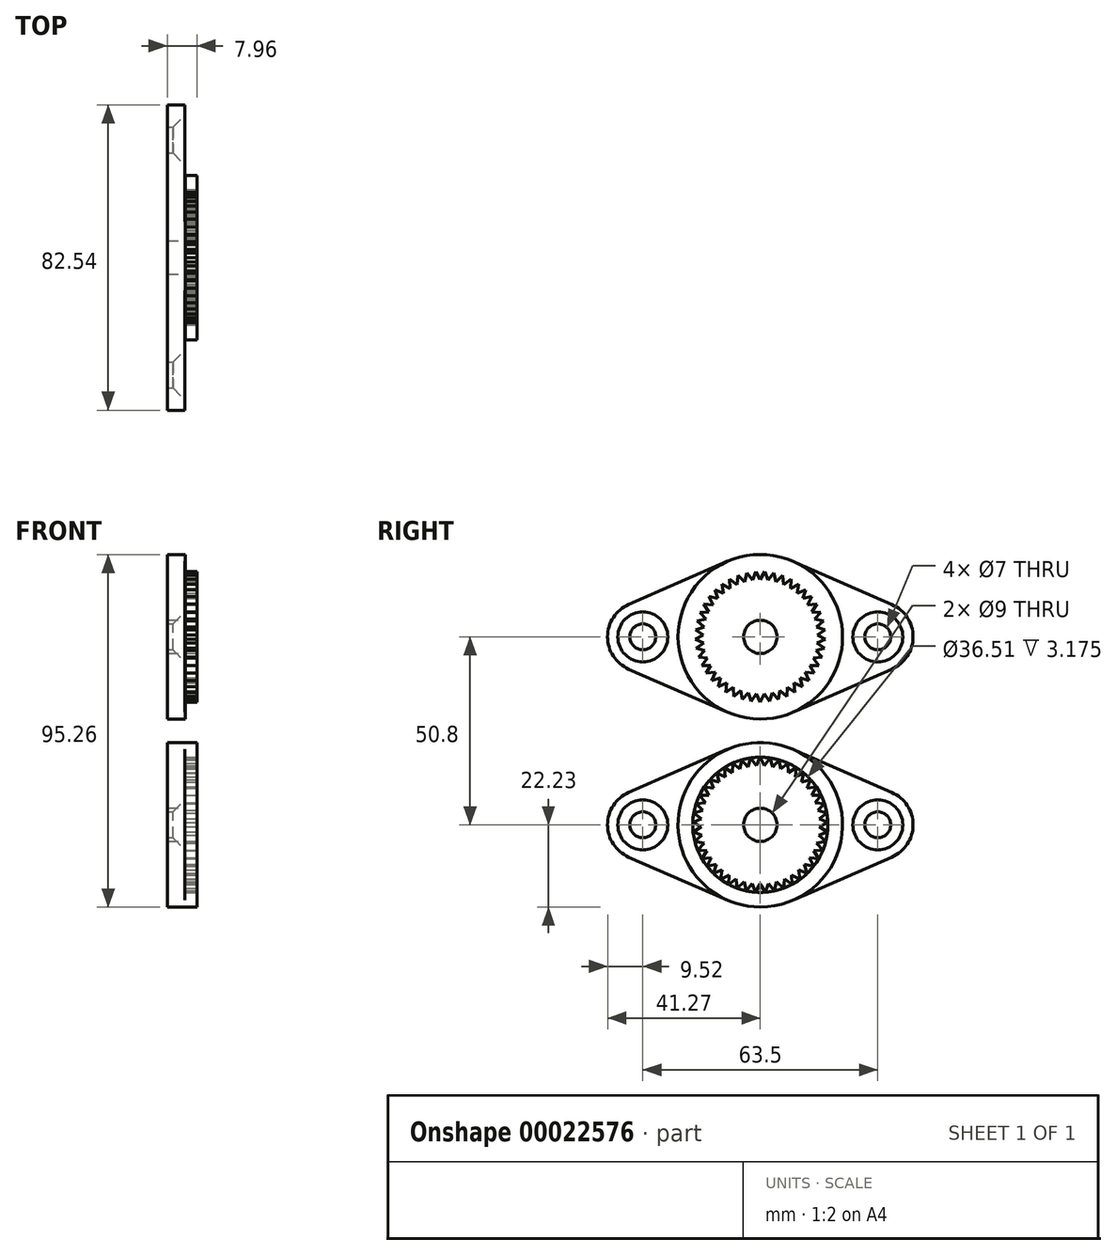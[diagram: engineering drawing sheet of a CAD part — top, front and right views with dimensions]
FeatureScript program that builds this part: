
annotation { "Feature Type Name" : "Feature", "Feature Type Description" : "" }
export const myFeature = defineFeature(function(context is Context, id is Id, definition is map)
    precondition{}
    {
        {
            var Q0;
            Q0=qCreatedBy(makeId("Right.planeOp"),FACE);
            var sketch = newSketch(context, id + "F0", { "sketchPlane" : qUnion([Q0])});
            skArc(sketch, "E0", {"start": v(-8.9, -20.37) * mm, "mid": v(0, -22.23) * mm, "end": v(8.9, -20.37) * mm});
            skLineSegment(sketch, "E1", {"start": v(-77.57, 0) * mm, "end": v(77.57, 0) * mm, "construction": true});
            skArc(sketch, "E2", {"start": v(-35.56, 8.73) * mm, "mid": v(-41.28, 0) * mm, "end": v(-35.56, -8.73) * mm});
            skArc(sketch, "E3", {"start": v(35.56, -8.73) * mm, "mid": v(41.27, 0) * mm, "end": v(35.56, 8.73) * mm});
            skLineSegment(sketch, "E4", {"start": v(-35.56, 8.73) * mm, "end": v(-8.89, 20.37) * mm});
            skLineSegment(sketch, "E5", {"start": v(-35.56, -8.73) * mm, "end": v(-8.9, -20.37) * mm});
            skLineSegment(sketch, "E6", {"start": v(35.56, -8.73) * mm, "end": v(8.9, -20.37) * mm});
            skLineSegment(sketch, "E7", {"start": v(35.56, 8.73) * mm, "end": v(8.89, 20.37) * mm});
            skArc(sketch, "E8.trimOffspring", {"start": v(8.9, 20.37) * mm, "mid": v(0, 22.22) * mm, "end": v(-8.9, 20.37) * mm});
            skLineSegment(sketch, "E9", {"start": v(-41.27, 0) * mm, "end": v(41.27, 0) * mm, "construction": true});
            skSolve(sketch);
        }
        {
            var Q0;
            Q0=qSketchRegion(id+"F0",true);
            extrude(context, id + "F1", {"entities" : qUnion([Q0]), "depth" : 4.76 * mm});
        }
        {
            var Q0;
            Q0=makeQuery(id+"F1.opExtrude","CAP_FACE",FACE,{"disambiguationData":[OSD([sQuery(id+"F0.wireOp",EDGE,"E0"),sQuery(id+"F0.wireOp",EDGE,"E2"),sQuery(id+"F0.wireOp",EDGE,"E3"),sQuery(id+"F0.wireOp",EDGE,"E4"),sQuery(id+"F0.wireOp",EDGE,"E5"),sQuery(id+"F0.wireOp",EDGE,"E6"),sQuery(id+"F0.wireOp",EDGE,"E7"),sQuery(id+"F0.wireOp",EDGE,"E8.trimOffspring")])],"isStart":false});
            var sketch = newSketch(context, id + "F2", { "sketchPlane" : qUnion([Q0])});
            skCircle(sketch, "E10", {"center": v(0, 0) * mm, "radius": 22.23 * mm});
            skSolve(sketch);
        }
        {
            var Q0;
            Q0=qSketchRegion(id+"F2",true);
            extrude(context, id + "F3", {"entities" : qUnion([Q0]), "operationType" : NewBodyOperationType.ADD, "depth" : 0.03 * mm});
        }
        {
            var Q0;
            Q0=qCreatedBy(makeId("Top.planeOp"),FACE);
            cPlane(context, id + "F4", {"entities" : qUnion([Q0]), "cplaneType" : CPlaneType.OFFSET, "offset" : 19.05 * mm, "width" : 152.4 * mm, "height" : 152.4 * mm});
        }
        {
            var Q0;
            Q0=qCreatedBy(makeId("Top.planeOp"),FACE);
            cPlane(context, id + "F5", {"entities" : qUnion([Q0]), "cplaneType" : CPlaneType.OFFSET, "offset" : 6.35 * mm, "width" : 152.4 * mm, "height" : 152.4 * mm});
        }
        {
            var Q0;
            Q0=qCreatedBy(id+"F4.planeOp",FACE);
            var sketch = newSketch(context, id + "F6", { "sketchPlane" : qUnion([Q0])});
            skLineSegment(sketch, "E11", {"start": v(0, 0) * mm, "end": v(4.79, 0) * mm, "construction": true});
            skLineSegment(sketch, "E12", {"start": v(4.79, 0.8) * mm, "end": v(4.79, -0.8) * mm});
            skLineSegment(sketch, "E13", {"start": v(4.79, 0) * mm, "end": v(5.8, 0) * mm, "construction": true});
            skLineSegment(sketch, "E14", {"start": v(4.79, -0.8) * mm, "end": v(5.8, 0) * mm});
            skLineSegment(sketch, "E15", {"start": v(4.79, 0.8) * mm, "end": v(5.8, 0) * mm});
            skSolve(sketch);
        }
        {
            var Q0;
            Q0=qCreatedBy(id+"F5.planeOp",FACE);
            var sketch = newSketch(context, id + "F7", { "sketchPlane" : qUnion([Q0])});
            skLineSegment(sketch, "E16", {"start": v(4.79, -0.25) * mm, "end": v(4.79, 0.25) * mm});
            skLineSegment(sketch, "E17", {"start": v(-1.93, 0) * mm, "end": v(4.79, 0) * mm, "construction": true});
            skLineSegment(sketch, "E18", {"start": v(4.79, 0) * mm, "end": v(5.8, 0) * mm, "construction": true});
            skLineSegment(sketch, "E19", {"start": v(5.8, 0) * mm, "end": v(4.79, 0.25) * mm});
            skLineSegment(sketch, "E20", {"start": v(5.8, 0) * mm, "end": v(4.79, -0.25) * mm});
            skSolve(sketch);
        }
        {
            var Q0;
            {var subQ0=sQuery(id+"F0.wireOp",EDGE,"E0");var subQ1=sQuery(id+"F0.wireOp",EDGE,"E3");var subQ2=sQuery(id+"F0.wireOp",EDGE,"E6");var subQ3=sQuery(id+"F0.wireOp",EDGE,"E7");var subQ4=sQuery(id+"F0.wireOp",EDGE,"E8.trimOffspring");Q0=makeQuery(id+"F3.boolean.opBoolean","SPLIT",FACE,{"disambiguationData":[TD([makeQuery(id+"F1.opExtrude","SWEPT_FACE",FACE,{"disambiguationData":[OSD([subQ1])]})])],"derivedFrom":makeQuery(id+"F1.opExtrude","CAP_FACE",FACE,{"disambiguationData":[OSD([subQ0,sQuery(id+"F0.wireOp",EDGE,"E2"),subQ1,sQuery(id+"F0.wireOp",EDGE,"E4"),sQuery(id+"F0.wireOp",EDGE,"E5"),subQ2,subQ3,subQ4])],"isStart":false})});}
            var sketch = newSketch(context, id + "F8", { "sketchPlane" : qUnion([Q0])});
            skCircle(sketch, "E21", {"center": v(31.75, 0) * mm, "radius": 3.5 * mm});
            skCircle(sketch, "E22", {"center": v(-31.75, 0) * mm, "radius": 3.5 * mm});
            skCircle(sketch, "E23", {"center": v(0, 0) * mm, "radius": 4.5 * mm});
            skSolve(sketch);
        }
        {
            var Q0;
            Q0=qSketchRegion(id+"F8",true);
            extrude(context, id + "F9", {"entities" : qUnion([Q0]), "operationType" : NewBodyOperationType.REMOVE, "endBound" : BoundingType.SYMMETRIC, "oppositeDirection" : true, "depth" : 25.4 * mm});
        }
        {
            var Q0;
            Q0=makeQuery(id+"F8.imprint","IMPRINT",FACE,{"disambiguationData":[TD([[makeQuery(id+"F8.imprint","IMPRINT",EDGE,{"derivedFrom":sQuery(id+"F8.wireOp",EDGE,"E21")}),-1.0]])]});
            var sketch = newSketch(context, id + "F10", { "sketchPlane" : qUnion([Q0])});
            skCircle(sketch, "E24", {"center": v(31.75, 0) * mm, "radius": 6.75 * mm});
            skCircle(sketch, "E25", {"center": v(-31.75, 0) * mm, "radius": 6.75 * mm});
            skSolve(sketch);
        }
        {
            var Q0;
            Q0=qSketchRegion(id+"F10",true);
            extrude(context, id + "F11", {"entities" : qUnion([Q0]), "operationType" : NewBodyOperationType.REMOVE, "oppositeDirection" : true, "depth" : 25.4 * mm, "hasDraft" : true, "draftAngle" : 45 * degree, "draftPullDirection" : true});
        }
        {
            var Q0;
            {var subQ0=sQuery(id+"F2.wireOp",EDGE,"E10");var subQ3=sQuery(id+"F0.wireOp",EDGE,"E6");Q0=makeQuery(id+"F3.boolean.opBoolean","SPLIT",EDGE,{"disambiguationData":[TD([makeQuery(id+"F1.opExtrude","SWEPT_FACE",FACE,{"disambiguationData":[OSD([subQ3])]})])],"derivedFrom":makeQuery(id+"F3.opExtrude","CAP_EDGE",EDGE,{"disambiguationData":[OSD([subQ0])],"isStart":true})});}
            var Q1;
            {var subQ0=sQuery(id+"F2.wireOp",EDGE,"E10");var subQ3=sQuery(id+"F0.wireOp",EDGE,"E4");Q1=makeQuery(id+"F3.boolean.opBoolean","SPLIT",EDGE,{"disambiguationData":[TD([makeQuery(id+"F1.opExtrude","SWEPT_FACE",FACE,{"disambiguationData":[OSD([subQ3])]})])],"derivedFrom":makeQuery(id+"F3.opExtrude","CAP_EDGE",EDGE,{"disambiguationData":[OSD([subQ0])],"isStart":true})});}
            fillet(context, id + "F12", {"entities" : qUnion([Q0, Q1]), "radius" : 0.8 * mm, "allowEdgeOverflow" : false});
        }
        {
            var Q0;
            Q0=makeQuery(id+"F3.opExtrude","CAP_FACE",FACE,{"disambiguationData":[OSD([sQuery(id+"F2.wireOp",EDGE,"E10")])],"isStart":false});
            var sketch = newSketch(context, id + "F13", { "sketchPlane" : qUnion([Q0])});
            skCircle(sketch, "E26", {"center": v(0, 0) * mm, "radius": 18.26 * mm});
            skCircle(sketch, "E27", {"center": v(0, 0) * mm, "radius": 22.23 * mm});
            skSolve(sketch);
        }
        {
            var Q0;
            Q0 = qSketchRegion(id + "F13", true);
            extrude(context, id + "F14", {"entities" : qUnion([Q0]), "operationType" : NewBodyOperationType.ADD, "depth" : 3.17 * mm});
        }
        {
            var Q0;
            Q0=makeQuery(id+"F1.opExtrude","SWEPT_BODY",BODY,{"disambiguationData":[OSD([sQuery(id+"F0.wireOp",EDGE,"E0"),sQuery(id+"F0.wireOp",EDGE,"E2"),sQuery(id+"F0.wireOp",EDGE,"E3"),sQuery(id+"F0.wireOp",EDGE,"E4"),sQuery(id+"F0.wireOp",EDGE,"E5"),sQuery(id+"F0.wireOp",EDGE,"E6"),sQuery(id+"F0.wireOp",EDGE,"E7"),sQuery(id+"F0.wireOp",EDGE,"E8.trimOffspring")])]});
            transform(context, id + "F15", {"entities" : qUnion([Q0]), "transformType" : TransformType.TRANSLATION_3D, "dx" : 0 * mm, "dy" : 0 * mm, "dz" : 50.8 * mm, "makeCopy" : true});
        }
        {
            var Q0;
            Q0=makeQuery(id+"F15.opPattern","COPY",FACE,{"derivedFrom":makeQuery(id+"F3.opExtrude","CAP_FACE",FACE,{"disambiguationData":[OSD([sQuery(id+"F2.wireOp",EDGE,"E10")])],"isStart":false}),"instanceName":"1"});
            var sketch = newSketch(context, id + "F16", { "sketchPlane" : qUnion([Q0])});
            skCircle(sketch, "E28", {"center": v(0, 50.8) * mm, "radius": 17.62 * mm});
            skCircle(sketch, "E29", {"center": v(0, 50.8) * mm, "radius": 4.5 * mm});
            skSolve(sketch);
        }
        {
            var Q0;
            Q0=makeQuery(id+"F15.opPattern","COPY",FACE,{"derivedFrom":makeQuery(id+"F14.opExtrude","CAP_FACE",FACE,{"disambiguationData":[OSD([sQuery(id+"F13.wireOp",EDGE,"E26"),sQuery(id+"F13.wireOp",EDGE,"E27")])],"isStart":false}),"instanceName":"1"});
            var sketch = newSketch(context, id + "F17", { "sketchPlane" : qUnion([Q0])});
            skCircle(sketch, "E30", {"center": v(0, 50.8) * mm, "radius": 18.26 * mm});
            skCircle(sketch, "E31", {"center": v(0, 50.8) * mm, "radius": 22.23 * mm});
            skSolve(sketch);
        }
        {
            var Q0;
            Q0 = qSketchRegion(id + "F17", true);
            var Q1;
            Q1=makeQuery(id+"F15.opPattern","COPY",FACE,{"derivedFrom":makeQuery(id+"F3.opExtrude","CAP_FACE",FACE,{"disambiguationData":[OSD([sQuery(id+"F2.wireOp",EDGE,"E10")])],"isStart":false}),"instanceName":"1"});
            extrude(context, id + "F18", {"entities" : qUnion([Q0]), "operationType" : NewBodyOperationType.REMOVE, "endBound" : BoundingType.UP_TO_SURFACE, "oppositeDirection" : true, "endBoundEntityFace" : qUnion([Q1]), "depth" : 25.4 * mm});
        }
        {
            var Q0;
            Q0 = qSketchRegion(id + "F16", true);
            extrude(context, id + "F19", {"entities" : qUnion([Q0]), "operationType" : NewBodyOperationType.ADD, "depth" : 3.17 * mm});
        }
        {
            var Q0;
            Q0=makeQuery(id+"F19.opExtrude","CAP_FACE",FACE,{"disambiguationData":[OSD([sQuery(id+"F16.wireOp",EDGE,"E28"),sQuery(id+"F16.wireOp",EDGE,"E29")])],"isStart":false});
            var sketch = newSketch(context, id + "F20", { "sketchPlane" : qUnion([Q0])});
            skLineSegment(sketch, "E32", {"start": v(0, 50.8) * mm, "end": v(0, 70.91) * mm, "construction": true});
            skArc(sketch, "E33", {"start": v(1.23, 68.38) * mm, "mid": v(0, 68.42) * mm, "end": v(-1.23, 68.38) * mm});
            skLineSegment(sketch, "E34", {"start": v(1.23, 68.38) * mm, "end": v(0, 50.8) * mm, "construction": true});
            skLineSegment(sketch, "E35", {"start": v(-1.23, 68.38) * mm, "end": v(0, 50.8) * mm, "construction": true});
            skLineSegment(sketch, "E36", {"start": v(1.23, 68.38) * mm, "end": v(0, 66.25) * mm});
            skLineSegment(sketch, "E37", {"start": v(0, 66.25) * mm, "end": v(-1.23, 68.38) * mm});
            skPoint(sketch, "E38.center", {"position": v(0, 0) * mm});
            skSolve(sketch);
        }
        {
            var Q0;
            Q0 = qSketchRegion(id + "F20", true);
            var Q1;
            Q1=makeQuery(id+"F18.boolean.opBoolean","MERGE",FACE,{"derivedFrom":[makeQuery(id+"F15.opPattern","COPY",FACE,{"derivedFrom":makeQuery(id+"F3.opExtrude","CAP_FACE",FACE,{"disambiguationData":[OSD([sQuery(id+"F2.wireOp",EDGE,"E10")])],"isStart":false}),"instanceName":"1"})],"fromTools":[makeQuery(id+"F18.opExtrude","CAP_FACE",FACE,{"disambiguationData":[OSD([sQuery(id+"F17.wireOp",EDGE,"E30"),sQuery(id+"F17.wireOp",EDGE,"E31")])],"isStart":false})]});
            extrude(context, id + "F21", {"entities" : qUnion([Q0]), "endBound" : BoundingType.UP_TO_SURFACE, "oppositeDirection" : true, "endBoundEntityFace" : qUnion([Q1]), "depth" : 25.4 * mm});
        }
        {
            var Q0;
            Q0=makeQuery(id+"F21.opExtrude","SWEPT_BODY",BODY,{"disambiguationData":[OSD([sQuery(id+"F20.wireOp",EDGE,"E33"),sQuery(id+"F20.wireOp",EDGE,"E36"),sQuery(id+"F20.wireOp",EDGE,"E37")])]});
            var Q1;
            Q1=makeQuery(id+"F19.opExtrude","CAP_EDGE",EDGE,{"disambiguationData":[OSD([sQuery(id+"F16.wireOp",EDGE,"E29")])],"isStart":false});
            circularPattern(context, id + "F22", {"entities" : qUnion([Q0]), "axis" : qUnion([Q1]), "angle" : 360 * degree, "instanceCount" : 45, "equalSpace" : true});
        }
        {
            var Q0;
            Q0=makeQuery(id+"F21.opExtrude","SWEPT_BODY",BODY,{"disambiguationData":[OSD([sQuery(id+"F20.wireOp",EDGE,"E33"),sQuery(id+"F20.wireOp",EDGE,"E36"),sQuery(id+"F20.wireOp",EDGE,"E37")])]});
            var Q1;
            Q1=makeQuery(id+"F22.opPattern","COPY",BODY,{"derivedFrom":makeQuery(id+"F21.opExtrude","SWEPT_BODY",BODY,{"disambiguationData":[OSD([sQuery(id+"F20.wireOp",EDGE,"E33"),sQuery(id+"F20.wireOp",EDGE,"E36"),sQuery(id+"F20.wireOp",EDGE,"E37")])]}),"instanceName":"71"});
            var Q2;
            Q2=makeQuery(id+"F22.opPattern","COPY",BODY,{"derivedFrom":makeQuery(id+"F21.opExtrude","SWEPT_BODY",BODY,{"disambiguationData":[OSD([sQuery(id+"F20.wireOp",EDGE,"E33"),sQuery(id+"F20.wireOp",EDGE,"E36"),sQuery(id+"F20.wireOp",EDGE,"E37")])]}),"instanceName":"70"});
            var Q3;
            Q3=makeQuery(id+"F22.opPattern","COPY",BODY,{"derivedFrom":makeQuery(id+"F21.opExtrude","SWEPT_BODY",BODY,{"disambiguationData":[OSD([sQuery(id+"F20.wireOp",EDGE,"E33"),sQuery(id+"F20.wireOp",EDGE,"E36"),sQuery(id+"F20.wireOp",EDGE,"E37")])]}),"instanceName":"68"});
            var Q4;
            Q4=makeQuery(id+"F22.opPattern","COPY",BODY,{"derivedFrom":makeQuery(id+"F21.opExtrude","SWEPT_BODY",BODY,{"disambiguationData":[OSD([sQuery(id+"F20.wireOp",EDGE,"E33"),sQuery(id+"F20.wireOp",EDGE,"E36"),sQuery(id+"F20.wireOp",EDGE,"E37")])]}),"instanceName":"69"});
            var Q5;
            Q5=makeQuery(id+"F22.opPattern","COPY",BODY,{"derivedFrom":makeQuery(id+"F21.opExtrude","SWEPT_BODY",BODY,{"disambiguationData":[OSD([sQuery(id+"F20.wireOp",EDGE,"E33"),sQuery(id+"F20.wireOp",EDGE,"E36"),sQuery(id+"F20.wireOp",EDGE,"E37")])]}),"instanceName":"67"});
            var Q6;
            Q6=makeQuery(id+"F22.opPattern","COPY",BODY,{"derivedFrom":makeQuery(id+"F21.opExtrude","SWEPT_BODY",BODY,{"disambiguationData":[OSD([sQuery(id+"F20.wireOp",EDGE,"E33"),sQuery(id+"F20.wireOp",EDGE,"E36"),sQuery(id+"F20.wireOp",EDGE,"E37")])]}),"instanceName":"1"});
            var Q7;
            Q7=makeQuery(id+"F22.opPattern","COPY",BODY,{"derivedFrom":makeQuery(id+"F21.opExtrude","SWEPT_BODY",BODY,{"disambiguationData":[OSD([sQuery(id+"F20.wireOp",EDGE,"E33"),sQuery(id+"F20.wireOp",EDGE,"E36"),sQuery(id+"F20.wireOp",EDGE,"E37")])]}),"instanceName":"2"});
            var Q8;
            Q8=makeQuery(id+"F22.opPattern","COPY",BODY,{"derivedFrom":makeQuery(id+"F21.opExtrude","SWEPT_BODY",BODY,{"disambiguationData":[OSD([sQuery(id+"F20.wireOp",EDGE,"E33"),sQuery(id+"F20.wireOp",EDGE,"E36"),sQuery(id+"F20.wireOp",EDGE,"E37")])]}),"instanceName":"66"});
            var Q9;
            Q9=makeQuery(id+"F22.opPattern","COPY",BODY,{"derivedFrom":makeQuery(id+"F21.opExtrude","SWEPT_BODY",BODY,{"disambiguationData":[OSD([sQuery(id+"F20.wireOp",EDGE,"E33"),sQuery(id+"F20.wireOp",EDGE,"E36"),sQuery(id+"F20.wireOp",EDGE,"E37")])]}),"instanceName":"65"});
            var Q10;
            Q10=makeQuery(id+"F22.opPattern","COPY",BODY,{"derivedFrom":makeQuery(id+"F21.opExtrude","SWEPT_BODY",BODY,{"disambiguationData":[OSD([sQuery(id+"F20.wireOp",EDGE,"E33"),sQuery(id+"F20.wireOp",EDGE,"E36"),sQuery(id+"F20.wireOp",EDGE,"E37")])]}),"instanceName":"63"});
            var Q11;
            Q11=makeQuery(id+"F22.opPattern","COPY",BODY,{"derivedFrom":makeQuery(id+"F21.opExtrude","SWEPT_BODY",BODY,{"disambiguationData":[OSD([sQuery(id+"F20.wireOp",EDGE,"E33"),sQuery(id+"F20.wireOp",EDGE,"E36"),sQuery(id+"F20.wireOp",EDGE,"E37")])]}),"instanceName":"62"});
            var Q12;
            Q12=makeQuery(id+"F22.opPattern","COPY",BODY,{"derivedFrom":makeQuery(id+"F21.opExtrude","SWEPT_BODY",BODY,{"disambiguationData":[OSD([sQuery(id+"F20.wireOp",EDGE,"E33"),sQuery(id+"F20.wireOp",EDGE,"E36"),sQuery(id+"F20.wireOp",EDGE,"E37")])]}),"instanceName":"64"});
            var Q13;
            Q13=makeQuery(id+"F22.opPattern","COPY",BODY,{"derivedFrom":makeQuery(id+"F21.opExtrude","SWEPT_BODY",BODY,{"disambiguationData":[OSD([sQuery(id+"F20.wireOp",EDGE,"E33"),sQuery(id+"F20.wireOp",EDGE,"E36"),sQuery(id+"F20.wireOp",EDGE,"E37")])]}),"instanceName":"61"});
            var Q14;
            Q14=makeQuery(id+"F22.opPattern","COPY",BODY,{"derivedFrom":makeQuery(id+"F21.opExtrude","SWEPT_BODY",BODY,{"disambiguationData":[OSD([sQuery(id+"F20.wireOp",EDGE,"E33"),sQuery(id+"F20.wireOp",EDGE,"E36"),sQuery(id+"F20.wireOp",EDGE,"E37")])]}),"instanceName":"60"});
            var Q15;
            Q15=makeQuery(id+"F22.opPattern","COPY",BODY,{"derivedFrom":makeQuery(id+"F21.opExtrude","SWEPT_BODY",BODY,{"disambiguationData":[OSD([sQuery(id+"F20.wireOp",EDGE,"E33"),sQuery(id+"F20.wireOp",EDGE,"E36"),sQuery(id+"F20.wireOp",EDGE,"E37")])]}),"instanceName":"59"});
            var Q16;
            Q16=makeQuery(id+"F22.opPattern","COPY",BODY,{"derivedFrom":makeQuery(id+"F21.opExtrude","SWEPT_BODY",BODY,{"disambiguationData":[OSD([sQuery(id+"F20.wireOp",EDGE,"E33"),sQuery(id+"F20.wireOp",EDGE,"E36"),sQuery(id+"F20.wireOp",EDGE,"E37")])]}),"instanceName":"58"});
            var Q17;
            Q17=makeQuery(id+"F22.opPattern","COPY",BODY,{"derivedFrom":makeQuery(id+"F21.opExtrude","SWEPT_BODY",BODY,{"disambiguationData":[OSD([sQuery(id+"F20.wireOp",EDGE,"E33"),sQuery(id+"F20.wireOp",EDGE,"E36"),sQuery(id+"F20.wireOp",EDGE,"E37")])]}),"instanceName":"56"});
            var Q18;
            Q18=makeQuery(id+"F22.opPattern","COPY",BODY,{"derivedFrom":makeQuery(id+"F21.opExtrude","SWEPT_BODY",BODY,{"disambiguationData":[OSD([sQuery(id+"F20.wireOp",EDGE,"E33"),sQuery(id+"F20.wireOp",EDGE,"E36"),sQuery(id+"F20.wireOp",EDGE,"E37")])]}),"instanceName":"55"});
            var Q19;
            Q19=makeQuery(id+"F22.opPattern","COPY",BODY,{"derivedFrom":makeQuery(id+"F21.opExtrude","SWEPT_BODY",BODY,{"disambiguationData":[OSD([sQuery(id+"F20.wireOp",EDGE,"E33"),sQuery(id+"F20.wireOp",EDGE,"E36"),sQuery(id+"F20.wireOp",EDGE,"E37")])]}),"instanceName":"53"});
            var Q20;
            Q20=makeQuery(id+"F22.opPattern","COPY",BODY,{"derivedFrom":makeQuery(id+"F21.opExtrude","SWEPT_BODY",BODY,{"disambiguationData":[OSD([sQuery(id+"F20.wireOp",EDGE,"E33"),sQuery(id+"F20.wireOp",EDGE,"E36"),sQuery(id+"F20.wireOp",EDGE,"E37")])]}),"instanceName":"51"});
            var Q21;
            Q21=makeQuery(id+"F22.opPattern","COPY",BODY,{"derivedFrom":makeQuery(id+"F21.opExtrude","SWEPT_BODY",BODY,{"disambiguationData":[OSD([sQuery(id+"F20.wireOp",EDGE,"E33"),sQuery(id+"F20.wireOp",EDGE,"E36"),sQuery(id+"F20.wireOp",EDGE,"E37")])]}),"instanceName":"49"});
            var Q22;
            Q22=makeQuery(id+"F22.opPattern","COPY",BODY,{"derivedFrom":makeQuery(id+"F21.opExtrude","SWEPT_BODY",BODY,{"disambiguationData":[OSD([sQuery(id+"F20.wireOp",EDGE,"E33"),sQuery(id+"F20.wireOp",EDGE,"E36"),sQuery(id+"F20.wireOp",EDGE,"E37")])]}),"instanceName":"57"});
            var Q23;
            Q23=makeQuery(id+"F22.opPattern","COPY",BODY,{"derivedFrom":makeQuery(id+"F21.opExtrude","SWEPT_BODY",BODY,{"disambiguationData":[OSD([sQuery(id+"F20.wireOp",EDGE,"E33"),sQuery(id+"F20.wireOp",EDGE,"E36"),sQuery(id+"F20.wireOp",EDGE,"E37")])]}),"instanceName":"54"});
            var Q24;
            Q24=makeQuery(id+"F22.opPattern","COPY",BODY,{"derivedFrom":makeQuery(id+"F21.opExtrude","SWEPT_BODY",BODY,{"disambiguationData":[OSD([sQuery(id+"F20.wireOp",EDGE,"E33"),sQuery(id+"F20.wireOp",EDGE,"E36"),sQuery(id+"F20.wireOp",EDGE,"E37")])]}),"instanceName":"52"});
            var Q25;
            Q25=makeQuery(id+"F22.opPattern","COPY",BODY,{"derivedFrom":makeQuery(id+"F21.opExtrude","SWEPT_BODY",BODY,{"disambiguationData":[OSD([sQuery(id+"F20.wireOp",EDGE,"E33"),sQuery(id+"F20.wireOp",EDGE,"E36"),sQuery(id+"F20.wireOp",EDGE,"E37")])]}),"instanceName":"50"});
            var Q26;
            Q26=makeQuery(id+"F22.opPattern","COPY",BODY,{"derivedFrom":makeQuery(id+"F21.opExtrude","SWEPT_BODY",BODY,{"disambiguationData":[OSD([sQuery(id+"F20.wireOp",EDGE,"E33"),sQuery(id+"F20.wireOp",EDGE,"E36"),sQuery(id+"F20.wireOp",EDGE,"E37")])]}),"instanceName":"48"});
            var Q27;
            Q27=makeQuery(id+"F22.opPattern","COPY",BODY,{"derivedFrom":makeQuery(id+"F21.opExtrude","SWEPT_BODY",BODY,{"disambiguationData":[OSD([sQuery(id+"F20.wireOp",EDGE,"E33"),sQuery(id+"F20.wireOp",EDGE,"E36"),sQuery(id+"F20.wireOp",EDGE,"E37")])]}),"instanceName":"47"});
            var Q28;
            Q28=makeQuery(id+"F22.opPattern","COPY",BODY,{"derivedFrom":makeQuery(id+"F21.opExtrude","SWEPT_BODY",BODY,{"disambiguationData":[OSD([sQuery(id+"F20.wireOp",EDGE,"E33"),sQuery(id+"F20.wireOp",EDGE,"E36"),sQuery(id+"F20.wireOp",EDGE,"E37")])]}),"instanceName":"44"});
            var Q29;
            Q29=makeQuery(id+"F22.opPattern","COPY",BODY,{"derivedFrom":makeQuery(id+"F21.opExtrude","SWEPT_BODY",BODY,{"disambiguationData":[OSD([sQuery(id+"F20.wireOp",EDGE,"E33"),sQuery(id+"F20.wireOp",EDGE,"E36"),sQuery(id+"F20.wireOp",EDGE,"E37")])]}),"instanceName":"42"});
            var Q30;
            Q30=makeQuery(id+"F22.opPattern","COPY",BODY,{"derivedFrom":makeQuery(id+"F21.opExtrude","SWEPT_BODY",BODY,{"disambiguationData":[OSD([sQuery(id+"F20.wireOp",EDGE,"E33"),sQuery(id+"F20.wireOp",EDGE,"E36"),sQuery(id+"F20.wireOp",EDGE,"E37")])]}),"instanceName":"45"});
            var Q31;
            Q31=makeQuery(id+"F22.opPattern","COPY",BODY,{"derivedFrom":makeQuery(id+"F21.opExtrude","SWEPT_BODY",BODY,{"disambiguationData":[OSD([sQuery(id+"F20.wireOp",EDGE,"E33"),sQuery(id+"F20.wireOp",EDGE,"E36"),sQuery(id+"F20.wireOp",EDGE,"E37")])]}),"instanceName":"40"});
            var Q32;
            Q32=makeQuery(id+"F22.opPattern","COPY",BODY,{"derivedFrom":makeQuery(id+"F21.opExtrude","SWEPT_BODY",BODY,{"disambiguationData":[OSD([sQuery(id+"F20.wireOp",EDGE,"E33"),sQuery(id+"F20.wireOp",EDGE,"E36"),sQuery(id+"F20.wireOp",EDGE,"E37")])]}),"instanceName":"38"});
            var Q33;
            Q33=makeQuery(id+"F22.opPattern","COPY",BODY,{"derivedFrom":makeQuery(id+"F21.opExtrude","SWEPT_BODY",BODY,{"disambiguationData":[OSD([sQuery(id+"F20.wireOp",EDGE,"E33"),sQuery(id+"F20.wireOp",EDGE,"E36"),sQuery(id+"F20.wireOp",EDGE,"E37")])]}),"instanceName":"37"});
            var Q34;
            Q34=makeQuery(id+"F22.opPattern","COPY",BODY,{"derivedFrom":makeQuery(id+"F21.opExtrude","SWEPT_BODY",BODY,{"disambiguationData":[OSD([sQuery(id+"F20.wireOp",EDGE,"E33"),sQuery(id+"F20.wireOp",EDGE,"E36"),sQuery(id+"F20.wireOp",EDGE,"E37")])]}),"instanceName":"36"});
            var Q35;
            Q35=makeQuery(id+"F22.opPattern","COPY",BODY,{"derivedFrom":makeQuery(id+"F21.opExtrude","SWEPT_BODY",BODY,{"disambiguationData":[OSD([sQuery(id+"F20.wireOp",EDGE,"E33"),sQuery(id+"F20.wireOp",EDGE,"E36"),sQuery(id+"F20.wireOp",EDGE,"E37")])]}),"instanceName":"33"});
            var Q36;
            Q36=makeQuery(id+"F22.opPattern","COPY",BODY,{"derivedFrom":makeQuery(id+"F21.opExtrude","SWEPT_BODY",BODY,{"disambiguationData":[OSD([sQuery(id+"F20.wireOp",EDGE,"E33"),sQuery(id+"F20.wireOp",EDGE,"E36"),sQuery(id+"F20.wireOp",EDGE,"E37")])]}),"instanceName":"28"});
            var Q37;
            Q37=makeQuery(id+"F22.opPattern","COPY",BODY,{"derivedFrom":makeQuery(id+"F21.opExtrude","SWEPT_BODY",BODY,{"disambiguationData":[OSD([sQuery(id+"F20.wireOp",EDGE,"E33"),sQuery(id+"F20.wireOp",EDGE,"E36"),sQuery(id+"F20.wireOp",EDGE,"E37")])]}),"instanceName":"29"});
            var Q38;
            Q38=makeQuery(id+"F22.opPattern","COPY",BODY,{"derivedFrom":makeQuery(id+"F21.opExtrude","SWEPT_BODY",BODY,{"disambiguationData":[OSD([sQuery(id+"F20.wireOp",EDGE,"E33"),sQuery(id+"F20.wireOp",EDGE,"E36"),sQuery(id+"F20.wireOp",EDGE,"E37")])]}),"instanceName":"30"});
            var Q39;
            Q39=makeQuery(id+"F22.opPattern","COPY",BODY,{"derivedFrom":makeQuery(id+"F21.opExtrude","SWEPT_BODY",BODY,{"disambiguationData":[OSD([sQuery(id+"F20.wireOp",EDGE,"E33"),sQuery(id+"F20.wireOp",EDGE,"E36"),sQuery(id+"F20.wireOp",EDGE,"E37")])]}),"instanceName":"31"});
            var Q40;
            Q40=makeQuery(id+"F22.opPattern","COPY",BODY,{"derivedFrom":makeQuery(id+"F21.opExtrude","SWEPT_BODY",BODY,{"disambiguationData":[OSD([sQuery(id+"F20.wireOp",EDGE,"E33"),sQuery(id+"F20.wireOp",EDGE,"E36"),sQuery(id+"F20.wireOp",EDGE,"E37")])]}),"instanceName":"32"});
            var Q41;
            Q41=makeQuery(id+"F22.opPattern","COPY",BODY,{"derivedFrom":makeQuery(id+"F21.opExtrude","SWEPT_BODY",BODY,{"disambiguationData":[OSD([sQuery(id+"F20.wireOp",EDGE,"E33"),sQuery(id+"F20.wireOp",EDGE,"E36"),sQuery(id+"F20.wireOp",EDGE,"E37")])]}),"instanceName":"34"});
            var Q42;
            Q42=makeQuery(id+"F22.opPattern","COPY",BODY,{"derivedFrom":makeQuery(id+"F21.opExtrude","SWEPT_BODY",BODY,{"disambiguationData":[OSD([sQuery(id+"F20.wireOp",EDGE,"E33"),sQuery(id+"F20.wireOp",EDGE,"E36"),sQuery(id+"F20.wireOp",EDGE,"E37")])]}),"instanceName":"35"});
            var Q43;
            Q43=makeQuery(id+"F22.opPattern","COPY",BODY,{"derivedFrom":makeQuery(id+"F21.opExtrude","SWEPT_BODY",BODY,{"disambiguationData":[OSD([sQuery(id+"F20.wireOp",EDGE,"E33"),sQuery(id+"F20.wireOp",EDGE,"E36"),sQuery(id+"F20.wireOp",EDGE,"E37")])]}),"instanceName":"3"});
            var Q44;
            Q44=makeQuery(id+"F22.opPattern","COPY",BODY,{"derivedFrom":makeQuery(id+"F21.opExtrude","SWEPT_BODY",BODY,{"disambiguationData":[OSD([sQuery(id+"F20.wireOp",EDGE,"E33"),sQuery(id+"F20.wireOp",EDGE,"E36"),sQuery(id+"F20.wireOp",EDGE,"E37")])]}),"instanceName":"4"});
            var Q45;
            Q45=makeQuery(id+"F22.opPattern","COPY",BODY,{"derivedFrom":makeQuery(id+"F21.opExtrude","SWEPT_BODY",BODY,{"disambiguationData":[OSD([sQuery(id+"F20.wireOp",EDGE,"E33"),sQuery(id+"F20.wireOp",EDGE,"E36"),sQuery(id+"F20.wireOp",EDGE,"E37")])]}),"instanceName":"5"});
            var Q46;
            Q46=makeQuery(id+"F22.opPattern","COPY",BODY,{"derivedFrom":makeQuery(id+"F21.opExtrude","SWEPT_BODY",BODY,{"disambiguationData":[OSD([sQuery(id+"F20.wireOp",EDGE,"E33"),sQuery(id+"F20.wireOp",EDGE,"E36"),sQuery(id+"F20.wireOp",EDGE,"E37")])]}),"instanceName":"6"});
            var Q47;
            Q47=makeQuery(id+"F22.opPattern","COPY",BODY,{"derivedFrom":makeQuery(id+"F21.opExtrude","SWEPT_BODY",BODY,{"disambiguationData":[OSD([sQuery(id+"F20.wireOp",EDGE,"E33"),sQuery(id+"F20.wireOp",EDGE,"E36"),sQuery(id+"F20.wireOp",EDGE,"E37")])]}),"instanceName":"8"});
            var Q48;
            Q48=makeQuery(id+"F22.opPattern","COPY",BODY,{"derivedFrom":makeQuery(id+"F21.opExtrude","SWEPT_BODY",BODY,{"disambiguationData":[OSD([sQuery(id+"F20.wireOp",EDGE,"E33"),sQuery(id+"F20.wireOp",EDGE,"E36"),sQuery(id+"F20.wireOp",EDGE,"E37")])]}),"instanceName":"9"});
            var Q49;
            Q49=makeQuery(id+"F22.opPattern","COPY",BODY,{"derivedFrom":makeQuery(id+"F21.opExtrude","SWEPT_BODY",BODY,{"disambiguationData":[OSD([sQuery(id+"F20.wireOp",EDGE,"E33"),sQuery(id+"F20.wireOp",EDGE,"E36"),sQuery(id+"F20.wireOp",EDGE,"E37")])]}),"instanceName":"10"});
            var Q50;
            Q50=makeQuery(id+"F22.opPattern","COPY",BODY,{"derivedFrom":makeQuery(id+"F21.opExtrude","SWEPT_BODY",BODY,{"disambiguationData":[OSD([sQuery(id+"F20.wireOp",EDGE,"E33"),sQuery(id+"F20.wireOp",EDGE,"E36"),sQuery(id+"F20.wireOp",EDGE,"E37")])]}),"instanceName":"12"});
            var Q51;
            Q51=makeQuery(id+"F22.opPattern","COPY",BODY,{"derivedFrom":makeQuery(id+"F21.opExtrude","SWEPT_BODY",BODY,{"disambiguationData":[OSD([sQuery(id+"F20.wireOp",EDGE,"E33"),sQuery(id+"F20.wireOp",EDGE,"E36"),sQuery(id+"F20.wireOp",EDGE,"E37")])]}),"instanceName":"14"});
            var Q52;
            Q52=makeQuery(id+"F22.opPattern","COPY",BODY,{"derivedFrom":makeQuery(id+"F21.opExtrude","SWEPT_BODY",BODY,{"disambiguationData":[OSD([sQuery(id+"F20.wireOp",EDGE,"E33"),sQuery(id+"F20.wireOp",EDGE,"E36"),sQuery(id+"F20.wireOp",EDGE,"E37")])]}),"instanceName":"7"});
            var Q53;
            Q53=makeQuery(id+"F22.opPattern","COPY",BODY,{"derivedFrom":makeQuery(id+"F21.opExtrude","SWEPT_BODY",BODY,{"disambiguationData":[OSD([sQuery(id+"F20.wireOp",EDGE,"E33"),sQuery(id+"F20.wireOp",EDGE,"E36"),sQuery(id+"F20.wireOp",EDGE,"E37")])]}),"instanceName":"13"});
            var Q54;
            Q54=makeQuery(id+"F22.opPattern","COPY",BODY,{"derivedFrom":makeQuery(id+"F21.opExtrude","SWEPT_BODY",BODY,{"disambiguationData":[OSD([sQuery(id+"F20.wireOp",EDGE,"E33"),sQuery(id+"F20.wireOp",EDGE,"E36"),sQuery(id+"F20.wireOp",EDGE,"E37")])]}),"instanceName":"15"});
            var Q55;
            Q55=makeQuery(id+"F22.opPattern","COPY",BODY,{"derivedFrom":makeQuery(id+"F21.opExtrude","SWEPT_BODY",BODY,{"disambiguationData":[OSD([sQuery(id+"F20.wireOp",EDGE,"E33"),sQuery(id+"F20.wireOp",EDGE,"E36"),sQuery(id+"F20.wireOp",EDGE,"E37")])]}),"instanceName":"16"});
            var Q56;
            Q56=makeQuery(id+"F22.opPattern","COPY",BODY,{"derivedFrom":makeQuery(id+"F21.opExtrude","SWEPT_BODY",BODY,{"disambiguationData":[OSD([sQuery(id+"F20.wireOp",EDGE,"E33"),sQuery(id+"F20.wireOp",EDGE,"E36"),sQuery(id+"F20.wireOp",EDGE,"E37")])]}),"instanceName":"17"});
            var Q57;
            Q57=makeQuery(id+"F22.opPattern","COPY",BODY,{"derivedFrom":makeQuery(id+"F21.opExtrude","SWEPT_BODY",BODY,{"disambiguationData":[OSD([sQuery(id+"F20.wireOp",EDGE,"E33"),sQuery(id+"F20.wireOp",EDGE,"E36"),sQuery(id+"F20.wireOp",EDGE,"E37")])]}),"instanceName":"19"});
            var Q58;
            Q58=makeQuery(id+"F22.opPattern","COPY",BODY,{"derivedFrom":makeQuery(id+"F21.opExtrude","SWEPT_BODY",BODY,{"disambiguationData":[OSD([sQuery(id+"F20.wireOp",EDGE,"E33"),sQuery(id+"F20.wireOp",EDGE,"E36"),sQuery(id+"F20.wireOp",EDGE,"E37")])]}),"instanceName":"21"});
            var Q59;
            Q59=makeQuery(id+"F22.opPattern","COPY",BODY,{"derivedFrom":makeQuery(id+"F21.opExtrude","SWEPT_BODY",BODY,{"disambiguationData":[OSD([sQuery(id+"F20.wireOp",EDGE,"E33"),sQuery(id+"F20.wireOp",EDGE,"E36"),sQuery(id+"F20.wireOp",EDGE,"E37")])]}),"instanceName":"24"});
            var Q60;
            Q60=makeQuery(id+"F22.opPattern","COPY",BODY,{"derivedFrom":makeQuery(id+"F21.opExtrude","SWEPT_BODY",BODY,{"disambiguationData":[OSD([sQuery(id+"F20.wireOp",EDGE,"E33"),sQuery(id+"F20.wireOp",EDGE,"E36"),sQuery(id+"F20.wireOp",EDGE,"E37")])]}),"instanceName":"46"});
            var Q61;
            Q61=makeQuery(id+"F22.opPattern","COPY",BODY,{"derivedFrom":makeQuery(id+"F21.opExtrude","SWEPT_BODY",BODY,{"disambiguationData":[OSD([sQuery(id+"F20.wireOp",EDGE,"E33"),sQuery(id+"F20.wireOp",EDGE,"E36"),sQuery(id+"F20.wireOp",EDGE,"E37")])]}),"instanceName":"43"});
            var Q62;
            Q62=makeQuery(id+"F22.opPattern","COPY",BODY,{"derivedFrom":makeQuery(id+"F21.opExtrude","SWEPT_BODY",BODY,{"disambiguationData":[OSD([sQuery(id+"F20.wireOp",EDGE,"E33"),sQuery(id+"F20.wireOp",EDGE,"E36"),sQuery(id+"F20.wireOp",EDGE,"E37")])]}),"instanceName":"41"});
            var Q63;
            Q63=makeQuery(id+"F22.opPattern","COPY",BODY,{"derivedFrom":makeQuery(id+"F21.opExtrude","SWEPT_BODY",BODY,{"disambiguationData":[OSD([sQuery(id+"F20.wireOp",EDGE,"E33"),sQuery(id+"F20.wireOp",EDGE,"E36"),sQuery(id+"F20.wireOp",EDGE,"E37")])]}),"instanceName":"39"});
            var Q64;
            Q64=makeQuery(id+"F22.opPattern","COPY",BODY,{"derivedFrom":makeQuery(id+"F21.opExtrude","SWEPT_BODY",BODY,{"disambiguationData":[OSD([sQuery(id+"F20.wireOp",EDGE,"E33"),sQuery(id+"F20.wireOp",EDGE,"E36"),sQuery(id+"F20.wireOp",EDGE,"E37")])]}),"instanceName":"27"});
            var Q65;
            Q65=makeQuery(id+"F22.opPattern","COPY",BODY,{"derivedFrom":makeQuery(id+"F21.opExtrude","SWEPT_BODY",BODY,{"disambiguationData":[OSD([sQuery(id+"F20.wireOp",EDGE,"E33"),sQuery(id+"F20.wireOp",EDGE,"E36"),sQuery(id+"F20.wireOp",EDGE,"E37")])]}),"instanceName":"26"});
            var Q66;
            Q66=makeQuery(id+"F22.opPattern","COPY",BODY,{"derivedFrom":makeQuery(id+"F21.opExtrude","SWEPT_BODY",BODY,{"disambiguationData":[OSD([sQuery(id+"F20.wireOp",EDGE,"E33"),sQuery(id+"F20.wireOp",EDGE,"E36"),sQuery(id+"F20.wireOp",EDGE,"E37")])]}),"instanceName":"23"});
            var Q67;
            Q67=makeQuery(id+"F22.opPattern","COPY",BODY,{"derivedFrom":makeQuery(id+"F21.opExtrude","SWEPT_BODY",BODY,{"disambiguationData":[OSD([sQuery(id+"F20.wireOp",EDGE,"E33"),sQuery(id+"F20.wireOp",EDGE,"E36"),sQuery(id+"F20.wireOp",EDGE,"E37")])]}),"instanceName":"22"});
            var Q68;
            Q68=makeQuery(id+"F22.opPattern","COPY",BODY,{"derivedFrom":makeQuery(id+"F21.opExtrude","SWEPT_BODY",BODY,{"disambiguationData":[OSD([sQuery(id+"F20.wireOp",EDGE,"E33"),sQuery(id+"F20.wireOp",EDGE,"E36"),sQuery(id+"F20.wireOp",EDGE,"E37")])]}),"instanceName":"18"});
            var Q69;
            Q69=makeQuery(id+"F22.opPattern","COPY",BODY,{"derivedFrom":makeQuery(id+"F21.opExtrude","SWEPT_BODY",BODY,{"disambiguationData":[OSD([sQuery(id+"F20.wireOp",EDGE,"E33"),sQuery(id+"F20.wireOp",EDGE,"E36"),sQuery(id+"F20.wireOp",EDGE,"E37")])]}),"instanceName":"25"});
            var Q70;
            Q70=makeQuery(id+"F22.opPattern","COPY",BODY,{"derivedFrom":makeQuery(id+"F21.opExtrude","SWEPT_BODY",BODY,{"disambiguationData":[OSD([sQuery(id+"F20.wireOp",EDGE,"E33"),sQuery(id+"F20.wireOp",EDGE,"E36"),sQuery(id+"F20.wireOp",EDGE,"E37")])]}),"instanceName":"20"});
            var Q71;
            Q71=makeQuery(id+"F22.opPattern","COPY",BODY,{"derivedFrom":makeQuery(id+"F21.opExtrude","SWEPT_BODY",BODY,{"disambiguationData":[OSD([sQuery(id+"F20.wireOp",EDGE,"E33"),sQuery(id+"F20.wireOp",EDGE,"E36"),sQuery(id+"F20.wireOp",EDGE,"E37")])]}),"instanceName":"11"});
            var Q72;
            Q72=makeQuery(id+"F15.opPattern","COPY",BODY,{"derivedFrom":makeQuery(id+"F1.opExtrude","SWEPT_BODY",BODY,{"disambiguationData":[OSD([sQuery(id+"F0.wireOp",EDGE,"E0"),sQuery(id+"F0.wireOp",EDGE,"E2"),sQuery(id+"F0.wireOp",EDGE,"E3"),sQuery(id+"F0.wireOp",EDGE,"E4"),sQuery(id+"F0.wireOp",EDGE,"E5"),sQuery(id+"F0.wireOp",EDGE,"E6"),sQuery(id+"F0.wireOp",EDGE,"E7"),sQuery(id+"F0.wireOp",EDGE,"E8.trimOffspring")])]}),"instanceName":"1"});
            booleanBodies(context, id + "F23", {"operationType" : BooleanOperationType.SUBTRACTION, "tools" : qUnion([Q0, Q1, Q2, Q3, Q4, Q5, Q6, Q7, Q8, Q9, Q10, Q11, Q12, Q13, Q14, Q15, Q16, Q17, Q18, Q19, Q20, Q21, Q22, Q23, Q24, Q25, Q26, Q27, Q28, Q29, Q30, Q31, Q32, Q33, Q34, Q35, Q36, Q37, Q38, Q39, Q40, Q41, Q42, Q43, Q44, Q45, Q46, Q47, Q48, Q49, Q50, Q51, Q52, Q53, Q54, Q55, Q56, Q57, Q58, Q59, Q60, Q61, Q62, Q63, Q64, Q65, Q66, Q67, Q68, Q69, Q70, Q71]), "targets" : qUnion([Q72])});
        }
        {
            var Q0;
            Q0=makeQuery(id+"F14.opExtrude","CAP_FACE",FACE,{"disambiguationData":[OSD([sQuery(id+"F13.wireOp",EDGE,"E26"),sQuery(id+"F13.wireOp",EDGE,"E27")])],"isStart":false});
            var sketch = newSketch(context, id + "F24", { "sketchPlane" : qUnion([Q0])});
            skLineSegment(sketch, "E39", {"start": v(0, 0) * mm, "end": v(0, 18.26) * mm, "construction": true});
            skLineSegment(sketch, "E40", {"start": v(0, 0) * mm, "end": v(1.27, 18.21) * mm, "construction": true});
            skArc(sketch, "E41", {"start": v(2.54, 18.08) * mm, "mid": v(1.27, 18.21) * mm, "end": v(0, 18.26) * mm});
            skLineSegment(sketch, "E42", {"start": v(2.54, 18.08) * mm, "end": v(0, 0) * mm, "construction": true});
            skLineSegment(sketch, "E43", {"start": v(2.54, 18.08) * mm, "end": v(1.12, 15.97) * mm});
            skLineSegment(sketch, "E44", {"start": v(1.12, 15.97) * mm, "end": v(0, 18.26) * mm});
            skSolve(sketch);
        }
        {
            var Q0;
            Q0 = qSketchRegion(id + "F24", true);
            var Q1;
            Q1=makeQuery(id+"F3.opExtrude","CAP_FACE",FACE,{"disambiguationData":[OSD([sQuery(id+"F2.wireOp",EDGE,"E10")])],"isStart":false});
            extrude(context, id + "F25", {"entities" : qUnion([Q0]), "endBound" : BoundingType.UP_TO_SURFACE, "oppositeDirection" : true, "endBoundEntityFace" : qUnion([Q1]), "depth" : 25.4 * mm});
        }
        {
            var Q0;
            Q0=makeQuery(id+"F25.opExtrude","SWEPT_BODY",BODY,{"disambiguationData":[OSD([sQuery(id+"F24.wireOp",EDGE,"E41"),sQuery(id+"F24.wireOp",EDGE,"E43"),sQuery(id+"F24.wireOp",EDGE,"E44")])]});
            var Q1;
            Q1=makeQuery(id+"F9.boolean.opBoolean","COPY",FACE,{"derivedFrom":makeQuery(id+"F9.opExtrude","SWEPT_FACE",FACE,{"disambiguationData":[OSD([sQuery(id+"F8.wireOp",EDGE,"E23")])]})});
            circularPattern(context, id + "F26", {"entities" : qUnion([Q0]), "axis" : qUnion([Q1]), "angle" : 8 * degree, "instanceCount" : 45});
        }
    });
